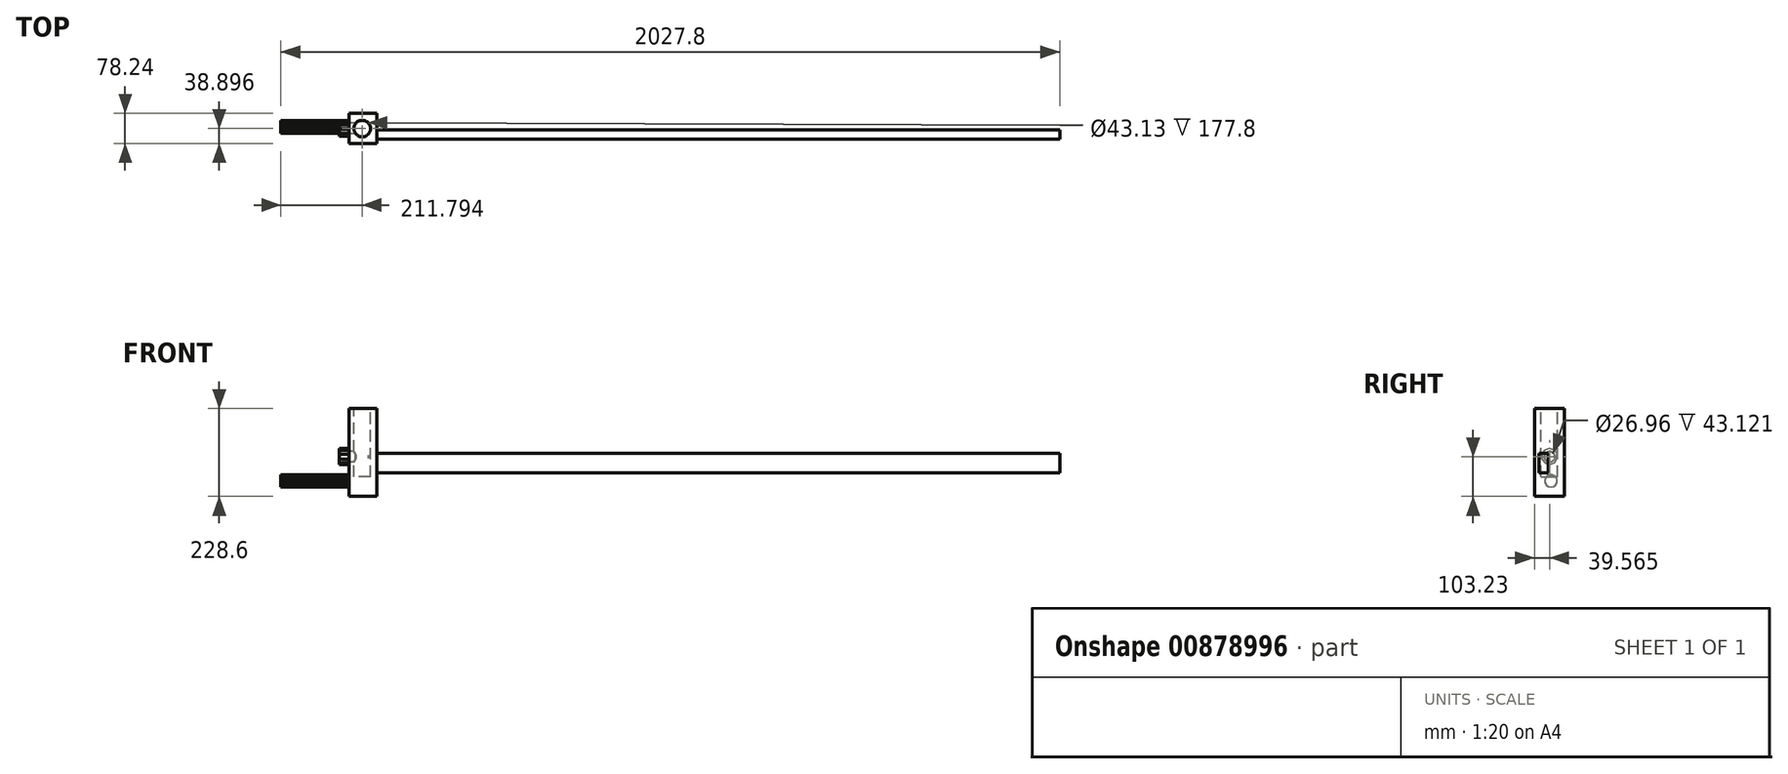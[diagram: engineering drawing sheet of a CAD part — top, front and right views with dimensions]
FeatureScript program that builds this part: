
annotation { "Feature Type Name" : "Feature", "Feature Type Description" : "" }
export const myFeature = defineFeature(function(context is Context, id is Id, definition is map)
    precondition{}
    {
        {
            var Q0;
            Q0=qCreatedBy(makeId("Top.planeOp"),FACE);
            var sketch = newSketch(context, id + "F0", { "sketchPlane" : qUnion([Q0])});
            skLineSegment(sketch, "E0.bottom", {"start": v(0, 0) * mm, "end": v(72, 0) * mm});
            skLineSegment(sketch, "E0.top", {"start": v(0, -78.24) * mm, "end": v(72, -78.24) * mm});
            skLineSegment(sketch, "E0.left", {"start": v(0, 0) * mm, "end": v(0, -78.24) * mm});
            skLineSegment(sketch, "E0.right", {"start": v(72, 0) * mm, "end": v(72, -78.24) * mm});
            skSolve(sketch);
        }
        {
            var Q0;
            Q0=makeQuery(id+"F0.imprint","IMPRINT",FACE,{"disambiguationData":[TD([[makeQuery(id+"F0.imprint","IMPRINT",EDGE,{"derivedFrom":sQuery(id+"F0.wireOp",EDGE,"E0.bottom")}),-1.0]])]});
            extrude(context, id + "F1", {"entities" : qUnion([Q0]), "depth" : 228.6 * mm, "offsetDistance" : 25.4 * mm});
        }
        {
            var Q0;
            Q0=makeQuery(id+"F1.opExtrude","SWEPT_FACE",FACE,{"disambiguationData":[OSD([sQuery(id+"F0.wireOp",EDGE,"E0.left")])]});
            var sketch = newSketch(context, id + "F2", { "sketchPlane" : qUnion([Q0])});
            skCircle(sketch, "E1.cCircle", {"center": v(39.34, 104.27) * mm, "radius": 19.66 * mm, "construction": true});
            skLineSegment(sketch, "E1.0", {"start": v(52.36, 120.33) * mm, "end": v(59.32, 109.6) * mm});
            skLineSegment(sketch, "E1.1", {"start": v(59.32, 109.6) * mm, "end": v(58.64, 96.85) * mm});
            skLineSegment(sketch, "E1.2", {"start": v(58.64, 96.85) * mm, "end": v(50.6, 86.92) * mm});
            skLineSegment(sketch, "E1.3", {"start": v(50.6, 86.92) * mm, "end": v(38.25, 83.62) * mm});
            skLineSegment(sketch, "E1.4", {"start": v(38.25, 83.62) * mm, "end": v(26.32, 88.2) * mm});
            skLineSegment(sketch, "E1.5", {"start": v(26.32, 88.2) * mm, "end": v(19.37, 98.93) * mm});
            skLineSegment(sketch, "E1.6", {"start": v(19.37, 98.93) * mm, "end": v(20.05, 111.69) * mm});
            skLineSegment(sketch, "E1.7", {"start": v(20.05, 111.69) * mm, "end": v(28.1, 121.61) * mm});
            skLineSegment(sketch, "E1.8", {"start": v(28.1, 121.61) * mm, "end": v(40.44, 124.91) * mm});
            skLineSegment(sketch, "E1.9", {"start": v(40.44, 124.91) * mm, "end": v(52.36, 120.33) * mm});
            skPoint(sketch, "E1.0.midPoint", {"position": v(55.84, 114.97) * mm});
            skSolve(sketch);
        }
        {
            var Q0;
            Q0 = qSketchRegion(id + "F2", true);
            extrude(context, id + "F3", {"entities" : qUnion([Q0]), "operationType" : NewBodyOperationType.ADD, "depth" : 25.4 * mm, "offsetDistance" : 25.4 * mm});
        }
        {
            var Q0;
            Q0=makeQuery(id+"F1.opExtrude","CAP_FACE",FACE,{"disambiguationData":[OSD([sQuery(id+"F0.wireOp",EDGE,"E0.bottom"),sQuery(id+"F0.wireOp",EDGE,"E0.top"),sQuery(id+"F0.wireOp",EDGE,"E0.left"),sQuery(id+"F0.wireOp",EDGE,"E0.right")])],"isStart":false});
            var sketch = newSketch(context, id + "F4", { "sketchPlane" : qUnion([Q0])});
            skCircle(sketch, "E2", {"center": v(34, -39.34) * mm, "radius": 21.57 * mm});
            skSolve(sketch);
        }
        {
            var Q0;
            Q0 = qSketchRegion(id + "F4", true);
            extrude(context, id + "F5", {"entities" : qUnion([Q0]), "operationType" : NewBodyOperationType.REMOVE, "oppositeDirection" : true, "depth" : 177.8 * mm, "offsetDistance" : 25.4 * mm});
        }
        {
            var Q0;
            Q0=makeQuery(id+"F3.opExtrude","CAP_FACE",FACE,{"disambiguationData":[OSD([sQuery(id+"F2.wireOp",EDGE,"E1.0"),sQuery(id+"F2.wireOp",EDGE,"E1.1"),sQuery(id+"F2.wireOp",EDGE,"E1.2"),sQuery(id+"F2.wireOp",EDGE,"E1.3"),sQuery(id+"F2.wireOp",EDGE,"E1.4"),sQuery(id+"F2.wireOp",EDGE,"E1.5"),sQuery(id+"F2.wireOp",EDGE,"E1.6"),sQuery(id+"F2.wireOp",EDGE,"E1.7"),sQuery(id+"F2.wireOp",EDGE,"E1.8"),sQuery(id+"F2.wireOp",EDGE,"E1.9")])],"isStart":false});
            var sketch = newSketch(context, id + "F6", { "sketchPlane" : qUnion([Q0])});
            skCircle(sketch, "E3", {"center": v(38.68, 103.23) * mm, "radius": 13.48 * mm});
            skPoint(sketch, "E3.centerSnap0", {"position": v(58.98, 103.23) * mm});
            skSolve(sketch);
        }
        {
            var Q0;
            Q0 = qSketchRegion(id + "F6", true);
            extrude(context, id + "F7", {"entities" : qUnion([Q0]), "operationType" : NewBodyOperationType.REMOVE, "oppositeDirection" : true, "depth" : 76.2 * mm, "offsetDistance" : 25.4 * mm});
        }
        {
            var Q0;
            Q0=makeQuery(id+"F1.opExtrude","SWEPT_FACE",FACE,{"disambiguationData":[OSD([sQuery(id+"F0.wireOp",EDGE,"E0.right")])]});
            var sketch = newSketch(context, id + "F8", { "sketchPlane" : qUnion([Q0])});
            skLineSegment(sketch, "E4.bottom", {"start": v(-42.46, 112.74) * mm, "end": v(-66.1, 112.74) * mm});
            skLineSegment(sketch, "E4.top", {"start": v(-42.46, 61.92) * mm, "end": v(-66.1, 61.92) * mm});
            skLineSegment(sketch, "E4.left", {"start": v(-42.46, 112.74) * mm, "end": v(-42.46, 61.92) * mm});
            skLineSegment(sketch, "E4.right", {"start": v(-66.1, 112.74) * mm, "end": v(-66.1, 61.92) * mm});
            skSolve(sketch);
        }
        {
            var Q0;
            Q0 = qSketchRegion(id + "F8", true);
            extrude(context, id + "F9", {"entities" : qUnion([Q0]), "operationType" : NewBodyOperationType.ADD, "depth" : 1778 * mm, "offsetDistance" : 25.4 * mm});
        }
        {
            var Q0;
            Q0=makeQuery(id+"F1.opExtrude","SWEPT_FACE",FACE,{"disambiguationData":[OSD([sQuery(id+"F0.wireOp",EDGE,"E0.left")])]});
            var sketch = newSketch(context, id + "F10", { "sketchPlane" : qUnion([Q0])});
            skCircle(sketch, "E5.cCircle", {"center": v(35.23, 40.82) * mm, "radius": 16 * mm, "construction": true});
            skLineSegment(sketch, "E5.0", {"start": v(31.83, 56.82) * mm, "end": v(38.63, 56.82) * mm});
            skLineSegment(sketch, "E5.1", {"start": v(38.63, 56.82) * mm, "end": v(44.84, 54.05) * mm});
            skLineSegment(sketch, "E5.2", {"start": v(44.84, 54.05) * mm, "end": v(49.4, 49) * mm});
            skLineSegment(sketch, "E5.3", {"start": v(49.4, 49) * mm, "end": v(51.5, 42.53) * mm});
            skLineSegment(sketch, "E5.4", {"start": v(51.5, 42.53) * mm, "end": v(50.79, 35.76) * mm});
            skLineSegment(sketch, "E5.5", {"start": v(50.79, 35.76) * mm, "end": v(47.39, 29.87) * mm});
            skLineSegment(sketch, "E5.6", {"start": v(47.39, 29.87) * mm, "end": v(41.88, 25.87) * mm});
            skLineSegment(sketch, "E5.7", {"start": v(41.88, 25.87) * mm, "end": v(35.23, 24.46) * mm});
            skLineSegment(sketch, "E5.8", {"start": v(35.23, 24.46) * mm, "end": v(28.58, 25.87) * mm});
            skLineSegment(sketch, "E5.9", {"start": v(28.58, 25.87) * mm, "end": v(23.07, 29.87) * mm});
            skLineSegment(sketch, "E5.10", {"start": v(23.07, 29.87) * mm, "end": v(19.67, 35.76) * mm});
            skLineSegment(sketch, "E5.11", {"start": v(19.67, 35.76) * mm, "end": v(18.96, 42.53) * mm});
            skLineSegment(sketch, "E5.12", {"start": v(18.96, 42.53) * mm, "end": v(21.06, 49) * mm});
            skLineSegment(sketch, "E5.13", {"start": v(21.06, 49) * mm, "end": v(25.61, 54.05) * mm});
            skLineSegment(sketch, "E5.14", {"start": v(25.61, 54.05) * mm, "end": v(31.83, 56.82) * mm});
            skPoint(sketch, "E5.0.midPoint", {"position": v(35.23, 56.82) * mm});
            skSolve(sketch);
        }
        {
            var Q0;
            Q0 = qSketchRegion(id + "F10", true);
            extrude(context, id + "F11", {"entities" : qUnion([Q0]), "operationType" : NewBodyOperationType.ADD, "depth" : 177.8 * mm, "offsetDistance" : 25.4 * mm});
        }
    });
